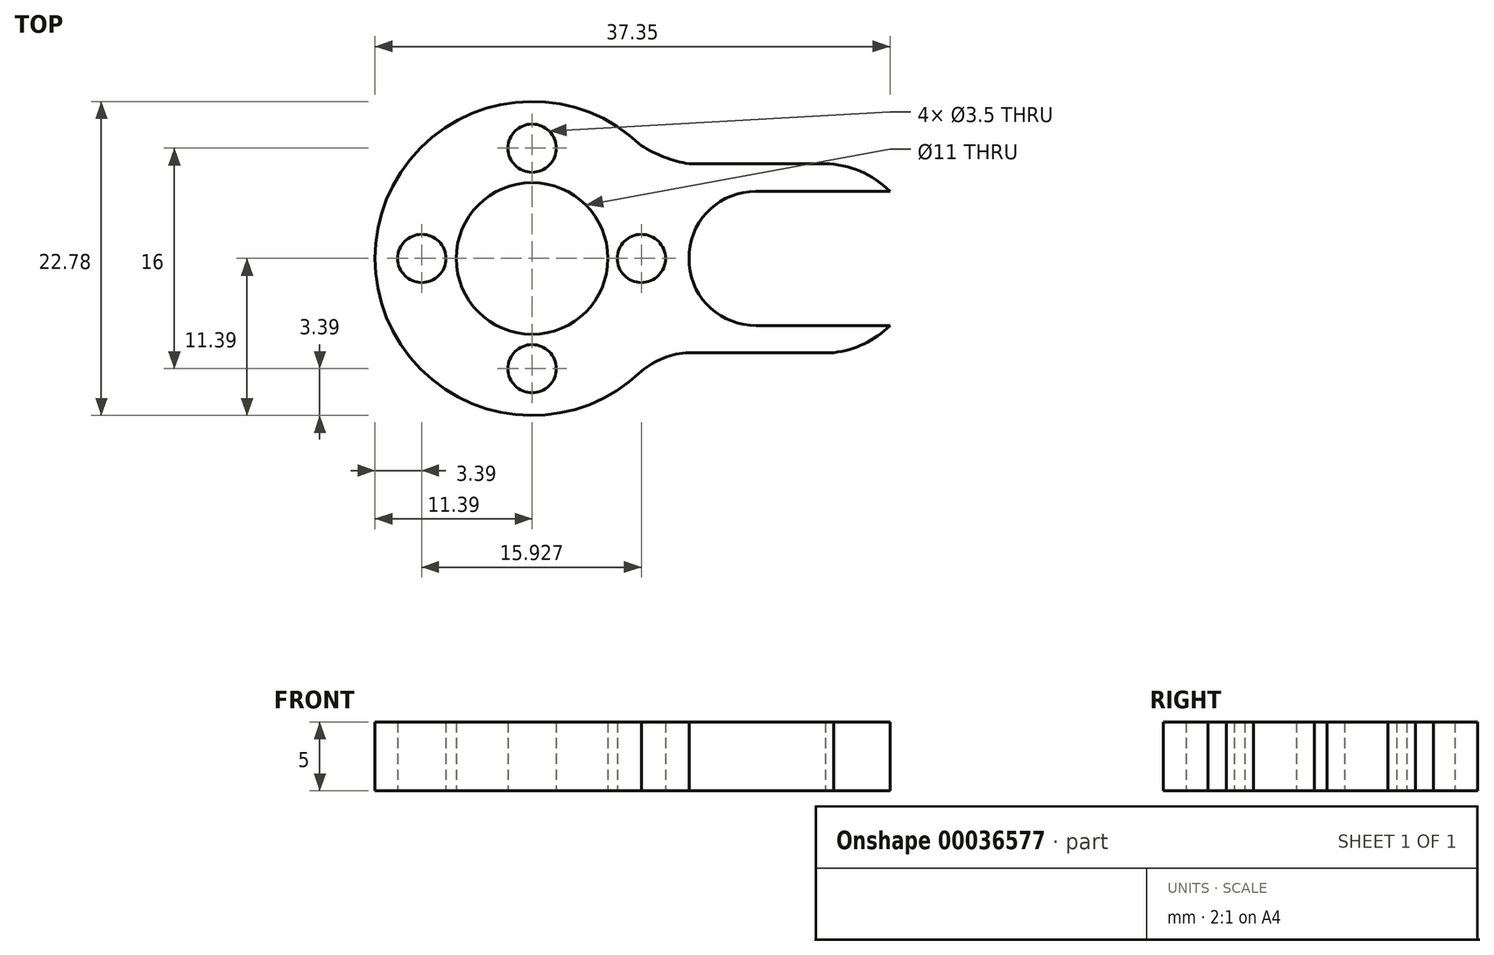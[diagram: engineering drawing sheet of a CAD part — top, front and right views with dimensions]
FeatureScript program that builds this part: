
annotation { "Feature Type Name" : "Feature", "Feature Type Description" : "" }
export const myFeature = defineFeature(function(context is Context, id is Id, definition is map)
    precondition{}
    {
        {
            var Q0;
            Q0=qCreatedBy(makeId("Top.planeOp"),FACE);
            var sketch = newSketch(context, id + "F0", { "sketchPlane" : qUnion([Q0])});
            skArc(sketch, "E0", {"start": v(7.93, 8.18) * mm, "mid": v(-11.4, 0) * mm, "end": v(7.93, -8.18) * mm});
            skCircle(sketch, "E1", {"center": v(0, 0) * mm, "radius": 5.5 * mm});
            skCircle(sketch, "E2", {"center": v(0, 8) * mm, "radius": 1.75 * mm});
            skCircle(sketch, "E3", {"center": v(-8, 0) * mm, "radius": 1.75 * mm});
            skCircle(sketch, "E4", {"center": v(0, -8) * mm, "radius": 1.75 * mm});
            skCircle(sketch, "E5", {"center": v(7.93, 0) * mm, "radius": 1.75 * mm});
            skArc(sketch, "E6", {"start": v(16.24, 4.87) * mm, "mid": v(12.95, 3.6) * mm, "end": v(11.38, 0.45) * mm});
            skArc(sketch, "E7", {"start": v(21.09, -4.87) * mm, "mid": v(21.11, -4.88) * mm, "end": v(21.14, -4.87) * mm});
            skArc(sketch, "E8", {"start": v(21.86, -6.83) * mm, "mid": v(24.08, -6.2) * mm, "end": v(25.96, -4.87) * mm});
            skLineSegment(sketch, "E9", {"start": v(21.26, 6.87) * mm, "end": v(11.38, 6.86) * mm});
            skLineSegment(sketch, "E10", {"start": v(21.86, -6.83) * mm, "end": v(11.38, -6.83) * mm});
            skLineSegment(sketch, "E11", {"start": v(16.26, -4.87) * mm, "end": v(25.96, -4.87) * mm});
            skLineSegment(sketch, "E12", {"start": v(25.96, 4.87) * mm, "end": v(16.24, 4.87) * mm});
            skLineSegment(sketch, "E13.trimOffspring", {"start": v(21.09, -4.87) * mm, "end": v(21.09, -4.87) * mm});
            skArc(sketch, "E14.trimOffspring", {"start": v(11.38, -0.45) * mm, "mid": v(12.96, -3.61) * mm, "end": v(16.26, -4.87) * mm});
            skArc(sketch, "E15.trimOffspring", {"start": v(25.96, 4.87) * mm, "mid": v(23.66, 6.39) * mm, "end": v(20.95, 6.87) * mm});
            skArc(sketch, "E16.trimOffspring", {"start": v(21.13, 4.87) * mm, "mid": v(21.1, 4.87) * mm, "end": v(21.07, 4.87) * mm});
            skArc(sketch, "E17", {"start": v(7.93, 8.18) * mm, "mid": v(9.6, 7.36) * mm, "end": v(11.38, 6.86) * mm});
            skArc(sketch, "E18", {"start": v(11.38, -6.83) * mm, "mid": v(9.55, -7.23) * mm, "end": v(7.93, -8.18) * mm});
            skArc(sketch, "E19.trimOffspring", {"start": v(11.38, -0.45) * mm, "mid": v(11.4, 0) * mm, "end": v(11.38, 0.45) * mm});
            skSolve(sketch);
        }
        {
            var Q0;
            Q0=makeQuery(id+"F0.imprint","IMPRINT",FACE,{"disambiguationData":[TD([[makeQuery(id+"F0.imprint","IMPRINT",EDGE,{"derivedFrom":sQuery(id+"F0.wireOp",EDGE,"E0")}),1.0]])]});
            var Q1;
            {var subQ9=sQuery(id+"F0.wireOp",EDGE,"E6");Q1=makeQuery(id+"F0.imprint","IMPRINT",FACE,{"disambiguationData":[TD([[makeQuery(id+"F0.imprint","IMPRINT",EDGE,{"derivedFrom":subQ9}),1.0]])]});}
            extrude(context, id + "F1", {"entities" : qUnion([Q0, Q1]), "depth" : 5 * mm});
        }
    });
